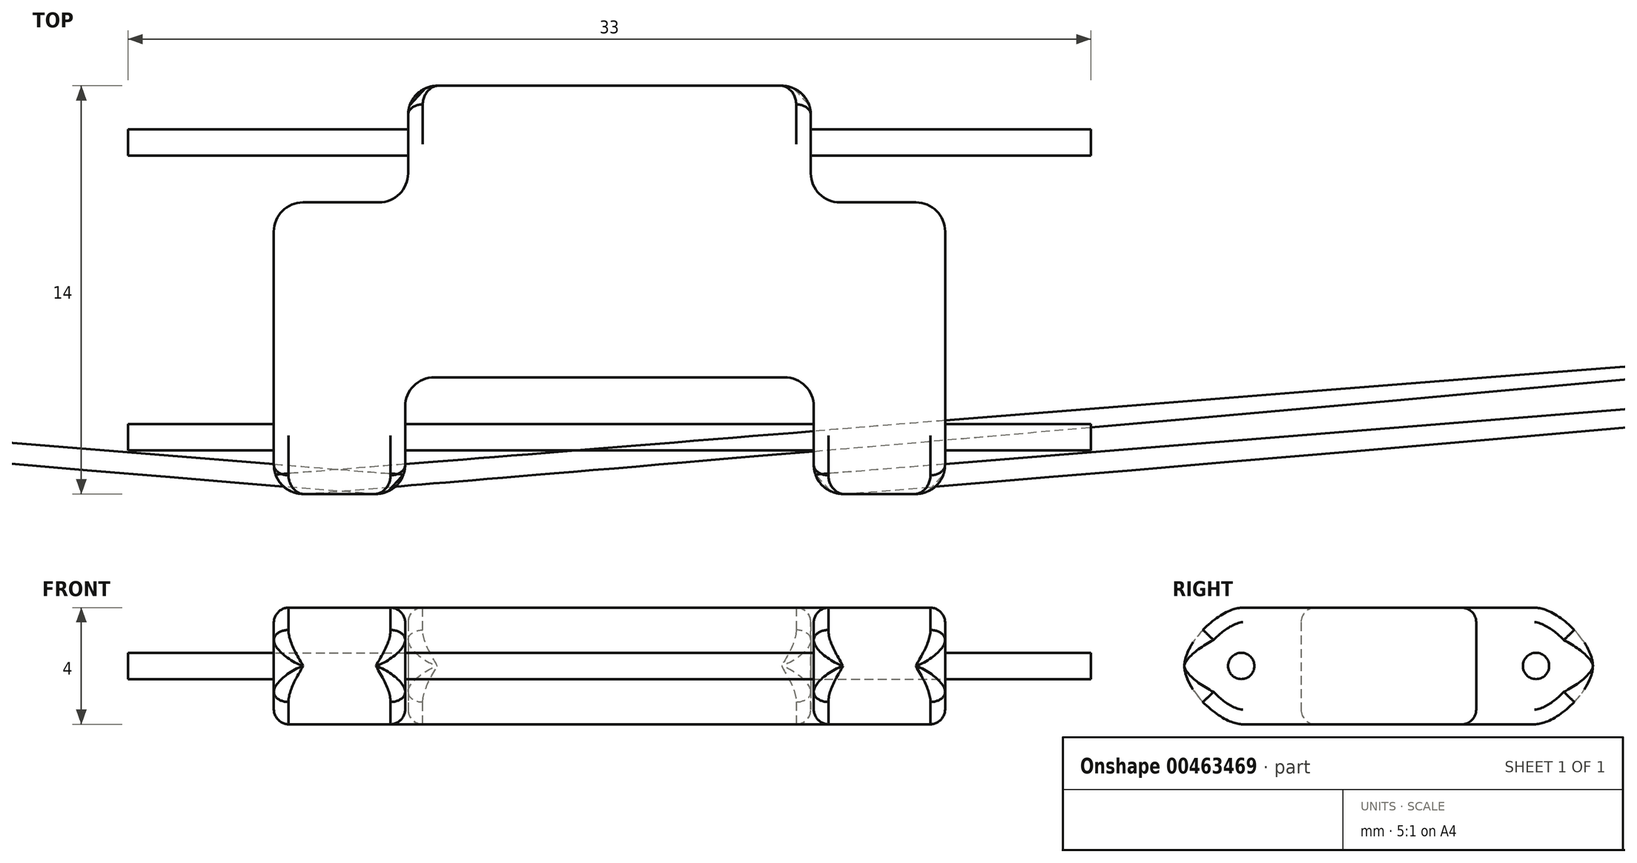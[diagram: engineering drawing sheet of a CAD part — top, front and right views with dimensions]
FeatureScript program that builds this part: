
annotation { "Feature Type Name" : "Feature", "Feature Type Description" : "" }
export const myFeature = defineFeature(function(context is Context, id is Id, definition is map)
    precondition{}
    {
        {
            var Q0;
            Q0=qCreatedBy(makeId("Top.planeOp"),FACE);
            var sketch = newSketch(context, id + "F0", { "sketchPlane" : qUnion([Q0])});
            skLineSegment(sketch, "E0", {"start": v(-1, -14) * mm, "end": v(-1, -10) * mm});
            skLineSegment(sketch, "E1", {"start": v(-1, -10) * mm, "end": v(-15, -10) * mm});
            skLineSegment(sketch, "E2", {"start": v(-15, -10) * mm, "end": v(-15, -14) * mm});
            skLineSegment(sketch, "E3", {"start": v(-15, -14) * mm, "end": v(-19.5, -14) * mm});
            skLineSegment(sketch, "E4", {"start": v(-1, -14) * mm, "end": v(3.5, -14) * mm});
            skLineSegment(sketch, "E5", {"start": v(-19.5, -14) * mm, "end": v(-19.5, -4) * mm});
            skLineSegment(sketch, "E6", {"start": v(-19.5, -4) * mm, "end": v(-14.9, -4) * mm});
            skLineSegment(sketch, "E7", {"start": v(-14.9, -4) * mm, "end": v(-14.9, 0) * mm});
            skLineSegment(sketch, "E8", {"start": v(-14.9, 0) * mm, "end": v(-1.1, 0) * mm});
            skLineSegment(sketch, "E9", {"start": v(-1.1, 0) * mm, "end": v(-1.1, -4) * mm});
            skLineSegment(sketch, "E10", {"start": v(-1.1, -4) * mm, "end": v(3.5, -4) * mm});
            skLineSegment(sketch, "E11", {"start": v(3.5, -4) * mm, "end": v(3.5, -14) * mm});
            skSolve(sketch);
        }
        {
            var Q0;
            Q0=makeQuery(id+"F0.imprint","IMPRINT",FACE,{"disambiguationData":[TD([[makeQuery(id+"F0.imprint","IMPRINT",EDGE,{"derivedFrom":sQuery(id+"F0.wireOp",EDGE,"E0")}),-1.0]])]});
            extrude(context, id + "F1", {"entities" : qUnion([Q0]), "depth" : 4 * mm, "offsetDistance" : 25 * mm});
        }
        {
            var Q0;
            Q0=makeQuery(id+"F1.opExtrude","SWEPT_EDGE",EDGE,{"disambiguationData":[OSD([sQuery(id+"F0.wireOp",EDGE,"JVpa2NSN-jCbz-SYZh-2br0-VPJ9OqO5sEDm"),sQuery(id+"F0.wireOp",EDGE,"TmuEh8Bb-qYGH-lmF9-es9h-PXmLGTj7apYS")])]});
            var Q1;
            Q1=makeQuery(id+"F1.opExtrude","SWEPT_EDGE",EDGE,{"disambiguationData":[OSD([sQuery(id+"F0.wireOp",EDGE,"Ta08JTOG-JjW1-DyQu-Rjfl-olB2hLuTZKrI"),sQuery(id+"F0.wireOp",EDGE,"5RLxsvr7-zWRq-nJ0O-23qe-XEgADmnkmLba")])]});
            var Q2;
            Q2=makeQuery(id+"F1.opExtrude","SWEPT_EDGE",EDGE,{"disambiguationData":[OSD([sQuery(id+"F0.wireOp",EDGE,"JVpa2NSN-jCbz-SYZh-2br0-VPJ9OqO5sEDm"),sQuery(id+"F0.wireOp",EDGE,"iIMMWLLX-5pRk-kAWc-YyXh-X3XYjQtiHgF8")])]});
            var Q3;
            Q3=makeQuery(id+"F1.opExtrude","SWEPT_EDGE",EDGE,{"disambiguationData":[OSD([sQuery(id+"F0.wireOp",EDGE,"Bp2VUUx9-f2Nf-Cqm2-FavC-f2X54JljXIIN"),sQuery(id+"F0.wireOp",EDGE,"TmuEh8Bb-qYGH-lmF9-es9h-PXmLGTj7apYS")])]});
            var Q4;
            Q4=makeQuery(id+"F1.opExtrude","SWEPT_EDGE",EDGE,{"disambiguationData":[OSD([sQuery(id+"F0.wireOp",EDGE,"aM0JYdi9-BpOH-c1Sx-eQZ7-4LdQcpM627Qa"),sQuery(id+"F0.wireOp",EDGE,"Ta08JTOG-JjW1-DyQu-Rjfl-olB2hLuTZKrI")])]});
            var Q5;
            Q5=makeQuery(id+"F1.opExtrude","SWEPT_EDGE",EDGE,{"disambiguationData":[OSD([sQuery(id+"F0.wireOp",EDGE,"5RLxsvr7-zWRq-nJ0O-23qe-XEgADmnkmLba"),sQuery(id+"F0.wireOp",EDGE,"Bp2VUUx9-f2Nf-Cqm2-FavC-f2X54JljXIIN")])]});
            var Q6;
            Q6=makeQuery(id+"F1.opExtrude","SWEPT_EDGE",EDGE,{"disambiguationData":[OSD([sQuery(id+"F0.wireOp",EDGE,"yeDMJLls-6pq1-5wso-vwFU-Q73Pk40JU32b"),sQuery(id+"F0.wireOp",EDGE,"aM0JYdi9-BpOH-c1Sx-eQZ7-4LdQcpM627Qa")])]});
            var Q7;
            Q7=makeQuery(id+"F1.opExtrude","SWEPT_EDGE",EDGE,{"disambiguationData":[OSD([sQuery(id+"F0.wireOp",EDGE,"yeDMJLls-6pq1-5wso-vwFU-Q73Pk40JU32b"),sQuery(id+"F0.wireOp",EDGE,"oADVPvip-QRiO-k2je-1GcM-0gCGYZzCVpqe")])]});
            var Q8;
            Q8=makeQuery(id+"F1.opExtrude","SWEPT_EDGE",EDGE,{"disambiguationData":[OSD([sQuery(id+"F0.wireOp",EDGE,"oADVPvip-QRiO-k2je-1GcM-0gCGYZzCVpqe"),sQuery(id+"F0.wireOp",EDGE,"10rlgXVg-n50c-kqx7-uExC-2RYqwfv1c7cX")])]});
            var Q9;
            Q9=makeQuery(id+"F1.opExtrude","SWEPT_EDGE",EDGE,{"disambiguationData":[OSD([sQuery(id+"F0.wireOp",EDGE,"TUznSBm0-cCe5-ovrQ-pSbA-vPagOil4q95r"),sQuery(id+"F0.wireOp",EDGE,"10rlgXVg-n50c-kqx7-uExC-2RYqwfv1c7cX")])]});
            var Q10;
            Q10=makeQuery(id+"F1.opExtrude","SWEPT_EDGE",EDGE,{"disambiguationData":[OSD([sQuery(id+"F0.wireOp",EDGE,"dIuJsfEi-w8Eu-UMFV-xWrQ-Q2fZL97E1xqK"),sQuery(id+"F0.wireOp",EDGE,"TUznSBm0-cCe5-ovrQ-pSbA-vPagOil4q95r")])]});
            var Q11;
            Q11=makeQuery(id+"F1.opExtrude","SWEPT_EDGE",EDGE,{"disambiguationData":[OSD([sQuery(id+"F0.wireOp",EDGE,"iIMMWLLX-5pRk-kAWc-YyXh-X3XYjQtiHgF8"),sQuery(id+"F0.wireOp",EDGE,"dIuJsfEi-w8Eu-UMFV-xWrQ-Q2fZL97E1xqK")])]});
            var Q12;
            Q12=makeQuery(id+"F1.opExtrude","SWEPT_EDGE",EDGE,{"disambiguationData":[OSD([sQuery(id+"F0.wireOp",EDGE,"yLF3BCVI-Jb2U-5dZP-aiB0-7200LCA53yiJ"),sQuery(id+"F0.wireOp",EDGE,"E3")])]});
            var Q13;
            Q13=makeQuery(id+"F1.opExtrude","SWEPT_EDGE",EDGE,{"disambiguationData":[OSD([sQuery(id+"F0.wireOp",EDGE,"E2"),sQuery(id+"F0.wireOp",EDGE,"E3")])]});
            var Q14;
            Q14=makeQuery(id+"F1.opExtrude","SWEPT_EDGE",EDGE,{"disambiguationData":[OSD([sQuery(id+"F0.wireOp",EDGE,"E1"),sQuery(id+"F0.wireOp",EDGE,"E2")])]});
            var Q15;
            Q15=makeQuery(id+"F1.opExtrude","SWEPT_EDGE",EDGE,{"disambiguationData":[OSD([sQuery(id+"F0.wireOp",EDGE,"E0"),sQuery(id+"F0.wireOp",EDGE,"E1")])]});
            var Q16;
            Q16=makeQuery(id+"F1.opExtrude","SWEPT_EDGE",EDGE,{"disambiguationData":[OSD([sQuery(id+"F0.wireOp",EDGE,"E0"),sQuery(id+"F0.wireOp",EDGE,"E4")])]});
            var Q17;
            Q17=makeQuery(id+"F1.opExtrude","SWEPT_EDGE",EDGE,{"disambiguationData":[OSD([sQuery(id+"F0.wireOp",EDGE,"W0sLsfjq-YAJu-qSV0-cM3q-n6XLMPe2tytr"),sQuery(id+"F0.wireOp",EDGE,"E4")])]});
            var Q18;
            Q18=makeQuery(id+"F1.opExtrude","SWEPT_EDGE",EDGE,{"disambiguationData":[OSD([sQuery(id+"F0.wireOp",EDGE,"E5"),sQuery(id+"F0.wireOp",EDGE,"E6")])]});
            var Q19;
            Q19=makeQuery(id+"F1.opExtrude","SWEPT_EDGE",EDGE,{"disambiguationData":[OSD([sQuery(id+"F0.wireOp",EDGE,"E6"),sQuery(id+"F0.wireOp",EDGE,"E7")])]});
            var Q20;
            Q20=makeQuery(id+"F1.opExtrude","SWEPT_EDGE",EDGE,{"disambiguationData":[OSD([sQuery(id+"F0.wireOp",EDGE,"E7"),sQuery(id+"F0.wireOp",EDGE,"E8")])]});
            var Q21;
            Q21=makeQuery(id+"F1.opExtrude","SWEPT_EDGE",EDGE,{"disambiguationData":[OSD([sQuery(id+"F0.wireOp",EDGE,"E8"),sQuery(id+"F0.wireOp",EDGE,"E9")])]});
            var Q22;
            Q22=makeQuery(id+"F1.opExtrude","SWEPT_EDGE",EDGE,{"disambiguationData":[OSD([sQuery(id+"F0.wireOp",EDGE,"E9"),sQuery(id+"F0.wireOp",EDGE,"E10")])]});
            var Q23;
            Q23=makeQuery(id+"F1.opExtrude","SWEPT_EDGE",EDGE,{"disambiguationData":[OSD([sQuery(id+"F0.wireOp",EDGE,"E10"),sQuery(id+"F0.wireOp",EDGE,"E11")])]});
            fillet(context, id + "F2", {"entities" : qUnion([Q0, Q1, Q2, Q3, Q4, Q5, Q6, Q7, Q8, Q9, Q10, Q11, Q12, Q13, Q14, Q15, Q16, Q17, Q18, Q19, Q20, Q21, Q22, Q23]), "radius" : 1 * mm, "tangentPropagation" : true, "allowEdgeOverflow" : false});
        }
        {
            var Q0;
            Q0=makeQuery(id+"F1.opExtrude","CAP_EDGE",EDGE,{"disambiguationData":[OSD([sQuery(id+"F0.wireOp",EDGE,"E8")])],"isStart":true});
            var Q1;
            Q1=makeQuery(id+"F1.opExtrude","CAP_EDGE",EDGE,{"disambiguationData":[OSD([sQuery(id+"F0.wireOp",EDGE,"E8")])],"isStart":false});
            var Q2;
            Q2=makeQuery(id+"F1.opExtrude","CAP_EDGE",EDGE,{"disambiguationData":[OSD([sQuery(id+"F0.wireOp",EDGE,"E3")])],"isStart":true});
            var Q3;
            Q3=makeQuery(id+"F1.opExtrude","CAP_EDGE",EDGE,{"disambiguationData":[OSD([sQuery(id+"F0.wireOp",EDGE,"E3")])],"isStart":false});
            var Q4;
            Q4=makeQuery(id+"F1.opExtrude","CAP_EDGE",EDGE,{"disambiguationData":[OSD([sQuery(id+"F0.wireOp",EDGE,"E4")])],"isStart":false});
            var Q5;
            Q5=makeQuery(id+"F1.opExtrude","CAP_EDGE",EDGE,{"disambiguationData":[OSD([sQuery(id+"F0.wireOp",EDGE,"E4")])],"isStart":true});
            fillet(context, id + "F3", {"entities" : qUnion([Q0, Q1, Q2, Q3, Q4, Q5]), "radius" : 2 * mm, "rho" : 0.3, "crossSection" : FilletCrossSection.CONIC, "allowEdgeOverflow" : false});
        }
        {
            var Q0;
            Q0=makeQuery(id+"F1.opExtrude","CAP_EDGE",EDGE,{"disambiguationData":[OSD([sQuery(id+"F0.wireOp",EDGE,"E1")])],"isStart":true});
            var Q1;
            {var subQ0=sQuery(id+"F0.wireOp",EDGE,"E2");var subQ1=sQuery(id+"F0.wireOp",EDGE,"E1");Q1=makeQuery(id+"F2.opFillet","BLEND_EDGE",EDGE,{"blendedFrom":[makeQuery(id+"F1.opExtrude","SWEPT_EDGE",EDGE,{"disambiguationData":[OSD([subQ1,subQ0])]}),makeQuery(id+"F1.opExtrude","CAP_FACE",FACE,{"disambiguationData":[OSD([sQuery(id+"F0.wireOp",EDGE,"E0"),subQ1,subQ0,sQuery(id+"F0.wireOp",EDGE,"E3"),sQuery(id+"F0.wireOp",EDGE,"E4"),sQuery(id+"F0.wireOp",EDGE,"E5"),sQuery(id+"F0.wireOp",EDGE,"E6"),sQuery(id+"F0.wireOp",EDGE,"E7"),sQuery(id+"F0.wireOp",EDGE,"E8"),sQuery(id+"F0.wireOp",EDGE,"E9"),sQuery(id+"F0.wireOp",EDGE,"E10"),sQuery(id+"F0.wireOp",EDGE,"E11")])],"isStart":true})],"blendedInto":[makeQuery(id+"F1.opExtrude","CAP_FACE",FACE,{"disambiguationData":[OSD([sQuery(id+"F0.wireOp",EDGE,"E0"),subQ1,subQ0,sQuery(id+"F0.wireOp",EDGE,"E3"),sQuery(id+"F0.wireOp",EDGE,"E4"),sQuery(id+"F0.wireOp",EDGE,"E5"),sQuery(id+"F0.wireOp",EDGE,"E6"),sQuery(id+"F0.wireOp",EDGE,"E7"),sQuery(id+"F0.wireOp",EDGE,"E8"),sQuery(id+"F0.wireOp",EDGE,"E9"),sQuery(id+"F0.wireOp",EDGE,"E10"),sQuery(id+"F0.wireOp",EDGE,"E11")])],"isStart":true})]});}
            var Q2;
            Q2=makeQuery(id+"F1.opExtrude","CAP_EDGE",EDGE,{"disambiguationData":[OSD([sQuery(id+"F0.wireOp",EDGE,"E2")])],"isStart":true});
            var Q3;
            Q3=makeQuery(id+"F3.opFillet","BLEND_EDGE",EDGE,{"blendedFrom":[makeQuery(id+"F1.opExtrude","CAP_EDGE",EDGE,{"disambiguationData":[OSD([sQuery(id+"F0.wireOp",EDGE,"E3")])],"isStart":true}),makeQuery(id+"F1.opExtrude","SWEPT_FACE",FACE,{"disambiguationData":[OSD([sQuery(id+"F0.wireOp",EDGE,"E2")])]})],"blendedInto":[makeQuery(id+"F1.opExtrude","SWEPT_FACE",FACE,{"disambiguationData":[OSD([sQuery(id+"F0.wireOp",EDGE,"E2")])]})]});
            var Q4;
            {var subQ0=sQuery(id+"F0.wireOp",EDGE,"E3");Q4=makeQuery(id+"F3.opFillet","BLEND_EDGE",EDGE,{"blendedFrom":[makeQuery(id+"F1.opExtrude","CAP_EDGE",EDGE,{"disambiguationData":[OSD([subQ0])],"isStart":true}),makeQuery(id+"F2.opFillet","BLEND_FACE",FACE,{"disambiguationData":[OSD([sQuery(id+"F0.wireOp",EDGE,"E2"),subQ0])]})],"blendedInto":[makeQuery(id+"F2.opFillet","BLEND_FACE",FACE,{"disambiguationData":[OSD([sQuery(id+"F0.wireOp",EDGE,"E2"),subQ0])]})]});}
            var Q5;
            {var subQ0=sQuery(id+"F0.wireOp",EDGE,"E1");var subQ1=sQuery(id+"F0.wireOp",EDGE,"E0");Q5=makeQuery(id+"F2.opFillet","BLEND_EDGE",EDGE,{"blendedFrom":[makeQuery(id+"F1.opExtrude","SWEPT_EDGE",EDGE,{"disambiguationData":[OSD([subQ1,subQ0])]}),makeQuery(id+"F1.opExtrude","CAP_FACE",FACE,{"disambiguationData":[OSD([subQ1,subQ0,sQuery(id+"F0.wireOp",EDGE,"E2"),sQuery(id+"F0.wireOp",EDGE,"E3"),sQuery(id+"F0.wireOp",EDGE,"E4"),sQuery(id+"F0.wireOp",EDGE,"E5"),sQuery(id+"F0.wireOp",EDGE,"E6"),sQuery(id+"F0.wireOp",EDGE,"E7"),sQuery(id+"F0.wireOp",EDGE,"E8"),sQuery(id+"F0.wireOp",EDGE,"E9"),sQuery(id+"F0.wireOp",EDGE,"E10"),sQuery(id+"F0.wireOp",EDGE,"E11")])],"isStart":true})],"blendedInto":[makeQuery(id+"F1.opExtrude","CAP_FACE",FACE,{"disambiguationData":[OSD([subQ1,subQ0,sQuery(id+"F0.wireOp",EDGE,"E2"),sQuery(id+"F0.wireOp",EDGE,"E3"),sQuery(id+"F0.wireOp",EDGE,"E4"),sQuery(id+"F0.wireOp",EDGE,"E5"),sQuery(id+"F0.wireOp",EDGE,"E6"),sQuery(id+"F0.wireOp",EDGE,"E7"),sQuery(id+"F0.wireOp",EDGE,"E8"),sQuery(id+"F0.wireOp",EDGE,"E9"),sQuery(id+"F0.wireOp",EDGE,"E10"),sQuery(id+"F0.wireOp",EDGE,"E11")])],"isStart":true})]});}
            var Q6;
            Q6=makeQuery(id+"F1.opExtrude","CAP_EDGE",EDGE,{"disambiguationData":[OSD([sQuery(id+"F0.wireOp",EDGE,"E0")])],"isStart":true});
            var Q7;
            {var subQ0=sQuery(id+"F0.wireOp",EDGE,"E4");Q7=makeQuery(id+"F3.opFillet","BLEND_EDGE",EDGE,{"blendedFrom":[makeQuery(id+"F1.opExtrude","CAP_EDGE",EDGE,{"disambiguationData":[OSD([subQ0])],"isStart":true}),makeQuery(id+"F2.opFillet","BLEND_FACE",FACE,{"disambiguationData":[OSD([sQuery(id+"F0.wireOp",EDGE,"E0"),subQ0])]})],"blendedInto":[makeQuery(id+"F2.opFillet","BLEND_FACE",FACE,{"disambiguationData":[OSD([sQuery(id+"F0.wireOp",EDGE,"E0"),subQ0])]})]});}
            var Q8;
            {var subQ0=sQuery(id+"F0.wireOp",EDGE,"E4");Q8=makeQuery(id+"F3.opFillet","BLEND_EDGE",EDGE,{"blendedFrom":[makeQuery(id+"F1.opExtrude","CAP_EDGE",EDGE,{"disambiguationData":[OSD([subQ0])],"isStart":false}),makeQuery(id+"F2.opFillet","BLEND_FACE",FACE,{"disambiguationData":[OSD([sQuery(id+"F0.wireOp",EDGE,"E0"),subQ0])]})],"blendedInto":[makeQuery(id+"F2.opFillet","BLEND_FACE",FACE,{"disambiguationData":[OSD([sQuery(id+"F0.wireOp",EDGE,"E0"),subQ0])]})]});}
            var Q9;
            {var subQ0=sQuery(id+"F0.wireOp",EDGE,"E3");Q9=makeQuery(id+"F3.opFillet","BLEND_EDGE",EDGE,{"blendedFrom":[makeQuery(id+"F1.opExtrude","CAP_EDGE",EDGE,{"disambiguationData":[OSD([subQ0])],"isStart":false}),makeQuery(id+"F2.opFillet","BLEND_FACE",FACE,{"disambiguationData":[OSD([sQuery(id+"F0.wireOp",EDGE,"E2"),subQ0])]})],"blendedInto":[makeQuery(id+"F2.opFillet","BLEND_FACE",FACE,{"disambiguationData":[OSD([sQuery(id+"F0.wireOp",EDGE,"E2"),subQ0])]})]});}
            var Q10;
            Q10=makeQuery(id+"F3.opFillet","BLEND_EDGE",EDGE,{"blendedFrom":[makeQuery(id+"F1.opExtrude","CAP_EDGE",EDGE,{"disambiguationData":[OSD([sQuery(id+"F0.wireOp",EDGE,"E3")])],"isStart":false}),makeQuery(id+"F1.opExtrude","SWEPT_FACE",FACE,{"disambiguationData":[OSD([sQuery(id+"F0.wireOp",EDGE,"E2")])]})],"blendedInto":[makeQuery(id+"F1.opExtrude","SWEPT_FACE",FACE,{"disambiguationData":[OSD([sQuery(id+"F0.wireOp",EDGE,"E2")])]})]});
            var Q11;
            Q11=makeQuery(id+"F1.opExtrude","CAP_EDGE",EDGE,{"disambiguationData":[OSD([sQuery(id+"F0.wireOp",EDGE,"E2")])],"isStart":false});
            var Q12;
            {var subQ0=sQuery(id+"F0.wireOp",EDGE,"E2");var subQ1=sQuery(id+"F0.wireOp",EDGE,"E1");Q12=makeQuery(id+"F2.opFillet","BLEND_EDGE",EDGE,{"blendedFrom":[makeQuery(id+"F1.opExtrude","SWEPT_EDGE",EDGE,{"disambiguationData":[OSD([subQ1,subQ0])]}),makeQuery(id+"F1.opExtrude","CAP_FACE",FACE,{"disambiguationData":[OSD([sQuery(id+"F0.wireOp",EDGE,"E0"),subQ1,subQ0,sQuery(id+"F0.wireOp",EDGE,"E3"),sQuery(id+"F0.wireOp",EDGE,"E4"),sQuery(id+"F0.wireOp",EDGE,"E5"),sQuery(id+"F0.wireOp",EDGE,"E6"),sQuery(id+"F0.wireOp",EDGE,"E7"),sQuery(id+"F0.wireOp",EDGE,"E8"),sQuery(id+"F0.wireOp",EDGE,"E9"),sQuery(id+"F0.wireOp",EDGE,"E10"),sQuery(id+"F0.wireOp",EDGE,"E11")])],"isStart":false})],"blendedInto":[makeQuery(id+"F1.opExtrude","CAP_FACE",FACE,{"disambiguationData":[OSD([sQuery(id+"F0.wireOp",EDGE,"E0"),subQ1,subQ0,sQuery(id+"F0.wireOp",EDGE,"E3"),sQuery(id+"F0.wireOp",EDGE,"E4"),sQuery(id+"F0.wireOp",EDGE,"E5"),sQuery(id+"F0.wireOp",EDGE,"E6"),sQuery(id+"F0.wireOp",EDGE,"E7"),sQuery(id+"F0.wireOp",EDGE,"E8"),sQuery(id+"F0.wireOp",EDGE,"E9"),sQuery(id+"F0.wireOp",EDGE,"E10"),sQuery(id+"F0.wireOp",EDGE,"E11")])],"isStart":false})]});}
            var Q13;
            Q13=makeQuery(id+"F1.opExtrude","CAP_EDGE",EDGE,{"disambiguationData":[OSD([sQuery(id+"F0.wireOp",EDGE,"E1")])],"isStart":false});
            var Q14;
            {var subQ0=sQuery(id+"F0.wireOp",EDGE,"E1");var subQ1=sQuery(id+"F0.wireOp",EDGE,"E0");Q14=makeQuery(id+"F2.opFillet","BLEND_EDGE",EDGE,{"blendedFrom":[makeQuery(id+"F1.opExtrude","SWEPT_EDGE",EDGE,{"disambiguationData":[OSD([subQ1,subQ0])]}),makeQuery(id+"F1.opExtrude","CAP_FACE",FACE,{"disambiguationData":[OSD([subQ1,subQ0,sQuery(id+"F0.wireOp",EDGE,"E2"),sQuery(id+"F0.wireOp",EDGE,"E3"),sQuery(id+"F0.wireOp",EDGE,"E4"),sQuery(id+"F0.wireOp",EDGE,"E5"),sQuery(id+"F0.wireOp",EDGE,"E6"),sQuery(id+"F0.wireOp",EDGE,"E7"),sQuery(id+"F0.wireOp",EDGE,"E8"),sQuery(id+"F0.wireOp",EDGE,"E9"),sQuery(id+"F0.wireOp",EDGE,"E10"),sQuery(id+"F0.wireOp",EDGE,"E11")])],"isStart":false})],"blendedInto":[makeQuery(id+"F1.opExtrude","CAP_FACE",FACE,{"disambiguationData":[OSD([subQ1,subQ0,sQuery(id+"F0.wireOp",EDGE,"E2"),sQuery(id+"F0.wireOp",EDGE,"E3"),sQuery(id+"F0.wireOp",EDGE,"E4"),sQuery(id+"F0.wireOp",EDGE,"E5"),sQuery(id+"F0.wireOp",EDGE,"E6"),sQuery(id+"F0.wireOp",EDGE,"E7"),sQuery(id+"F0.wireOp",EDGE,"E8"),sQuery(id+"F0.wireOp",EDGE,"E9"),sQuery(id+"F0.wireOp",EDGE,"E10"),sQuery(id+"F0.wireOp",EDGE,"E11")])],"isStart":false})]});}
            var Q15;
            Q15=makeQuery(id+"F1.opExtrude","CAP_EDGE",EDGE,{"disambiguationData":[OSD([sQuery(id+"F0.wireOp",EDGE,"E0")])],"isStart":false});
            var Q16;
            Q16=makeQuery(id+"F3.opFillet","BLEND_EDGE",EDGE,{"blendedFrom":[makeQuery(id+"F1.opExtrude","CAP_EDGE",EDGE,{"disambiguationData":[OSD([sQuery(id+"F0.wireOp",EDGE,"E4")])],"isStart":false}),makeQuery(id+"F1.opExtrude","SWEPT_FACE",FACE,{"disambiguationData":[OSD([sQuery(id+"F0.wireOp",EDGE,"E0")])]})],"blendedInto":[makeQuery(id+"F1.opExtrude","SWEPT_FACE",FACE,{"disambiguationData":[OSD([sQuery(id+"F0.wireOp",EDGE,"E0")])]})]});
            var Q17;
            Q17=makeQuery(id+"F3.opFillet","BLEND_EDGE",EDGE,{"blendedFrom":[makeQuery(id+"F1.opExtrude","CAP_EDGE",EDGE,{"disambiguationData":[OSD([sQuery(id+"F0.wireOp",EDGE,"E4")])],"isStart":true}),makeQuery(id+"F1.opExtrude","SWEPT_FACE",FACE,{"disambiguationData":[OSD([sQuery(id+"F0.wireOp",EDGE,"E0")])]})],"blendedInto":[makeQuery(id+"F1.opExtrude","SWEPT_FACE",FACE,{"disambiguationData":[OSD([sQuery(id+"F0.wireOp",EDGE,"E0")])]})]});
            var Q18;
            {var subQ0=sQuery(id+"F0.wireOp",EDGE,"E3");Q18=makeQuery(id+"F3.opFillet","BLEND_EDGE",EDGE,{"blendedFrom":[makeQuery(id+"F1.opExtrude","CAP_EDGE",EDGE,{"disambiguationData":[OSD([subQ0])],"isStart":false}),makeQuery(id+"F2.opFillet","BLEND_FACE",FACE,{"disambiguationData":[OSD([subQ0,sQuery(id+"F0.wireOp",EDGE,"E5")])]})],"blendedInto":[makeQuery(id+"F2.opFillet","BLEND_FACE",FACE,{"disambiguationData":[OSD([subQ0,sQuery(id+"F0.wireOp",EDGE,"E5")])]})]});}
            var Q19;
            {var subQ0=sQuery(id+"F0.wireOp",EDGE,"E3");Q19=makeQuery(id+"F3.opFillet","BLEND_EDGE",EDGE,{"blendedFrom":[makeQuery(id+"F1.opExtrude","CAP_EDGE",EDGE,{"disambiguationData":[OSD([subQ0])],"isStart":true}),makeQuery(id+"F2.opFillet","BLEND_FACE",FACE,{"disambiguationData":[OSD([subQ0,sQuery(id+"F0.wireOp",EDGE,"E5")])]})],"blendedInto":[makeQuery(id+"F2.opFillet","BLEND_FACE",FACE,{"disambiguationData":[OSD([subQ0,sQuery(id+"F0.wireOp",EDGE,"E5")])]})]});}
            var Q20;
            Q20=makeQuery(id+"F1.opExtrude","CAP_EDGE",EDGE,{"disambiguationData":[OSD([sQuery(id+"F0.wireOp",EDGE,"E5")])],"isStart":true});
            var Q21;
            Q21=makeQuery(id+"F3.opFillet","BLEND_EDGE",EDGE,{"blendedFrom":[makeQuery(id+"F1.opExtrude","CAP_EDGE",EDGE,{"disambiguationData":[OSD([sQuery(id+"F0.wireOp",EDGE,"E3")])],"isStart":true}),makeQuery(id+"F1.opExtrude","SWEPT_FACE",FACE,{"disambiguationData":[OSD([sQuery(id+"F0.wireOp",EDGE,"E5")])]})],"blendedInto":[makeQuery(id+"F1.opExtrude","SWEPT_FACE",FACE,{"disambiguationData":[OSD([sQuery(id+"F0.wireOp",EDGE,"E5")])]})]});
            var Q22;
            Q22=makeQuery(id+"F3.opFillet","BLEND_EDGE",EDGE,{"blendedFrom":[makeQuery(id+"F1.opExtrude","CAP_EDGE",EDGE,{"disambiguationData":[OSD([sQuery(id+"F0.wireOp",EDGE,"E3")])],"isStart":false}),makeQuery(id+"F1.opExtrude","SWEPT_FACE",FACE,{"disambiguationData":[OSD([sQuery(id+"F0.wireOp",EDGE,"E5")])]})],"blendedInto":[makeQuery(id+"F1.opExtrude","SWEPT_FACE",FACE,{"disambiguationData":[OSD([sQuery(id+"F0.wireOp",EDGE,"E5")])]})]});
            var Q23;
            Q23=makeQuery(id+"F1.opExtrude","CAP_EDGE",EDGE,{"disambiguationData":[OSD([sQuery(id+"F0.wireOp",EDGE,"E5")])],"isStart":false});
            var Q24;
            {var subQ0=sQuery(id+"F0.wireOp",EDGE,"E6");var subQ1=sQuery(id+"F0.wireOp",EDGE,"E5");Q24=makeQuery(id+"F2.opFillet","BLEND_EDGE",EDGE,{"blendedFrom":[makeQuery(id+"F1.opExtrude","SWEPT_EDGE",EDGE,{"disambiguationData":[OSD([subQ1,subQ0])]}),makeQuery(id+"F1.opExtrude","CAP_FACE",FACE,{"disambiguationData":[OSD([sQuery(id+"F0.wireOp",EDGE,"E0"),sQuery(id+"F0.wireOp",EDGE,"E1"),sQuery(id+"F0.wireOp",EDGE,"E2"),sQuery(id+"F0.wireOp",EDGE,"E3"),sQuery(id+"F0.wireOp",EDGE,"E4"),subQ1,subQ0,sQuery(id+"F0.wireOp",EDGE,"E7"),sQuery(id+"F0.wireOp",EDGE,"E8"),sQuery(id+"F0.wireOp",EDGE,"E9"),sQuery(id+"F0.wireOp",EDGE,"E10"),sQuery(id+"F0.wireOp",EDGE,"E11")])],"isStart":false})],"blendedInto":[makeQuery(id+"F1.opExtrude","CAP_FACE",FACE,{"disambiguationData":[OSD([sQuery(id+"F0.wireOp",EDGE,"E0"),sQuery(id+"F0.wireOp",EDGE,"E1"),sQuery(id+"F0.wireOp",EDGE,"E2"),sQuery(id+"F0.wireOp",EDGE,"E3"),sQuery(id+"F0.wireOp",EDGE,"E4"),subQ1,subQ0,sQuery(id+"F0.wireOp",EDGE,"E7"),sQuery(id+"F0.wireOp",EDGE,"E8"),sQuery(id+"F0.wireOp",EDGE,"E9"),sQuery(id+"F0.wireOp",EDGE,"E10"),sQuery(id+"F0.wireOp",EDGE,"E11")])],"isStart":false})]});}
            var Q25;
            {var subQ0=sQuery(id+"F0.wireOp",EDGE,"E6");var subQ1=sQuery(id+"F0.wireOp",EDGE,"E5");Q25=makeQuery(id+"F2.opFillet","BLEND_EDGE",EDGE,{"blendedFrom":[makeQuery(id+"F1.opExtrude","SWEPT_EDGE",EDGE,{"disambiguationData":[OSD([subQ1,subQ0])]}),makeQuery(id+"F1.opExtrude","CAP_FACE",FACE,{"disambiguationData":[OSD([sQuery(id+"F0.wireOp",EDGE,"E0"),sQuery(id+"F0.wireOp",EDGE,"E1"),sQuery(id+"F0.wireOp",EDGE,"E2"),sQuery(id+"F0.wireOp",EDGE,"E3"),sQuery(id+"F0.wireOp",EDGE,"E4"),subQ1,subQ0,sQuery(id+"F0.wireOp",EDGE,"E7"),sQuery(id+"F0.wireOp",EDGE,"E8"),sQuery(id+"F0.wireOp",EDGE,"E9"),sQuery(id+"F0.wireOp",EDGE,"E10"),sQuery(id+"F0.wireOp",EDGE,"E11")])],"isStart":true})],"blendedInto":[makeQuery(id+"F1.opExtrude","CAP_FACE",FACE,{"disambiguationData":[OSD([sQuery(id+"F0.wireOp",EDGE,"E0"),sQuery(id+"F0.wireOp",EDGE,"E1"),sQuery(id+"F0.wireOp",EDGE,"E2"),sQuery(id+"F0.wireOp",EDGE,"E3"),sQuery(id+"F0.wireOp",EDGE,"E4"),subQ1,subQ0,sQuery(id+"F0.wireOp",EDGE,"E7"),sQuery(id+"F0.wireOp",EDGE,"E8"),sQuery(id+"F0.wireOp",EDGE,"E9"),sQuery(id+"F0.wireOp",EDGE,"E10"),sQuery(id+"F0.wireOp",EDGE,"E11")])],"isStart":true})]});}
            var Q26;
            Q26=makeQuery(id+"F1.opExtrude","CAP_EDGE",EDGE,{"disambiguationData":[OSD([sQuery(id+"F0.wireOp",EDGE,"E6")])],"isStart":true});
            var Q27;
            Q27=makeQuery(id+"F1.opExtrude","CAP_EDGE",EDGE,{"disambiguationData":[OSD([sQuery(id+"F0.wireOp",EDGE,"E6")])],"isStart":false});
            var Q28;
            {var subQ0=sQuery(id+"F0.wireOp",EDGE,"E7");var subQ1=sQuery(id+"F0.wireOp",EDGE,"E6");Q28=makeQuery(id+"F2.opFillet","BLEND_EDGE",EDGE,{"blendedFrom":[makeQuery(id+"F1.opExtrude","SWEPT_EDGE",EDGE,{"disambiguationData":[OSD([subQ1,subQ0])]}),makeQuery(id+"F1.opExtrude","CAP_FACE",FACE,{"disambiguationData":[OSD([sQuery(id+"F0.wireOp",EDGE,"E0"),sQuery(id+"F0.wireOp",EDGE,"E1"),sQuery(id+"F0.wireOp",EDGE,"E2"),sQuery(id+"F0.wireOp",EDGE,"E3"),sQuery(id+"F0.wireOp",EDGE,"E4"),sQuery(id+"F0.wireOp",EDGE,"E5"),subQ1,subQ0,sQuery(id+"F0.wireOp",EDGE,"E8"),sQuery(id+"F0.wireOp",EDGE,"E9"),sQuery(id+"F0.wireOp",EDGE,"E10"),sQuery(id+"F0.wireOp",EDGE,"E11")])],"isStart":false})],"blendedInto":[makeQuery(id+"F1.opExtrude","CAP_FACE",FACE,{"disambiguationData":[OSD([sQuery(id+"F0.wireOp",EDGE,"E0"),sQuery(id+"F0.wireOp",EDGE,"E1"),sQuery(id+"F0.wireOp",EDGE,"E2"),sQuery(id+"F0.wireOp",EDGE,"E3"),sQuery(id+"F0.wireOp",EDGE,"E4"),sQuery(id+"F0.wireOp",EDGE,"E5"),subQ1,subQ0,sQuery(id+"F0.wireOp",EDGE,"E8"),sQuery(id+"F0.wireOp",EDGE,"E9"),sQuery(id+"F0.wireOp",EDGE,"E10"),sQuery(id+"F0.wireOp",EDGE,"E11")])],"isStart":false})]});}
            var Q29;
            {var subQ0=sQuery(id+"F0.wireOp",EDGE,"E7");var subQ1=sQuery(id+"F0.wireOp",EDGE,"E6");Q29=makeQuery(id+"F2.opFillet","BLEND_EDGE",EDGE,{"blendedFrom":[makeQuery(id+"F1.opExtrude","SWEPT_EDGE",EDGE,{"disambiguationData":[OSD([subQ1,subQ0])]}),makeQuery(id+"F1.opExtrude","CAP_FACE",FACE,{"disambiguationData":[OSD([sQuery(id+"F0.wireOp",EDGE,"E0"),sQuery(id+"F0.wireOp",EDGE,"E1"),sQuery(id+"F0.wireOp",EDGE,"E2"),sQuery(id+"F0.wireOp",EDGE,"E3"),sQuery(id+"F0.wireOp",EDGE,"E4"),sQuery(id+"F0.wireOp",EDGE,"E5"),subQ1,subQ0,sQuery(id+"F0.wireOp",EDGE,"E8"),sQuery(id+"F0.wireOp",EDGE,"E9"),sQuery(id+"F0.wireOp",EDGE,"E10"),sQuery(id+"F0.wireOp",EDGE,"E11")])],"isStart":true})],"blendedInto":[makeQuery(id+"F1.opExtrude","CAP_FACE",FACE,{"disambiguationData":[OSD([sQuery(id+"F0.wireOp",EDGE,"E0"),sQuery(id+"F0.wireOp",EDGE,"E1"),sQuery(id+"F0.wireOp",EDGE,"E2"),sQuery(id+"F0.wireOp",EDGE,"E3"),sQuery(id+"F0.wireOp",EDGE,"E4"),sQuery(id+"F0.wireOp",EDGE,"E5"),subQ1,subQ0,sQuery(id+"F0.wireOp",EDGE,"E8"),sQuery(id+"F0.wireOp",EDGE,"E9"),sQuery(id+"F0.wireOp",EDGE,"E10"),sQuery(id+"F0.wireOp",EDGE,"E11")])],"isStart":true})]});}
            var Q30;
            Q30=makeQuery(id+"F3.opFillet","BLEND_EDGE",EDGE,{"blendedFrom":[makeQuery(id+"F1.opExtrude","CAP_EDGE",EDGE,{"disambiguationData":[OSD([sQuery(id+"F0.wireOp",EDGE,"E8")])],"isStart":false}),makeQuery(id+"F1.opExtrude","SWEPT_FACE",FACE,{"disambiguationData":[OSD([sQuery(id+"F0.wireOp",EDGE,"E7")])]})],"blendedInto":[makeQuery(id+"F1.opExtrude","SWEPT_FACE",FACE,{"disambiguationData":[OSD([sQuery(id+"F0.wireOp",EDGE,"E7")])]})]});
            var Q31;
            Q31=makeQuery(id+"F1.opExtrude","CAP_EDGE",EDGE,{"disambiguationData":[OSD([sQuery(id+"F0.wireOp",EDGE,"E7")])],"isStart":false});
            var Q32;
            {var subQ0=sQuery(id+"F0.wireOp",EDGE,"E8");Q32=makeQuery(id+"F3.opFillet","BLEND_EDGE",EDGE,{"blendedFrom":[makeQuery(id+"F1.opExtrude","CAP_EDGE",EDGE,{"disambiguationData":[OSD([subQ0])],"isStart":false}),makeQuery(id+"F2.opFillet","BLEND_FACE",FACE,{"disambiguationData":[OSD([sQuery(id+"F0.wireOp",EDGE,"E7"),subQ0])]})],"blendedInto":[makeQuery(id+"F2.opFillet","BLEND_FACE",FACE,{"disambiguationData":[OSD([sQuery(id+"F0.wireOp",EDGE,"E7"),subQ0])]})]});}
            var Q33;
            {var subQ0=sQuery(id+"F0.wireOp",EDGE,"E8");Q33=makeQuery(id+"F3.opFillet","BLEND_EDGE",EDGE,{"blendedFrom":[makeQuery(id+"F1.opExtrude","CAP_EDGE",EDGE,{"disambiguationData":[OSD([subQ0])],"isStart":true}),makeQuery(id+"F2.opFillet","BLEND_FACE",FACE,{"disambiguationData":[OSD([sQuery(id+"F0.wireOp",EDGE,"E7"),subQ0])]})],"blendedInto":[makeQuery(id+"F2.opFillet","BLEND_FACE",FACE,{"disambiguationData":[OSD([sQuery(id+"F0.wireOp",EDGE,"E7"),subQ0])]})]});}
            var Q34;
            Q34=makeQuery(id+"F3.opFillet","BLEND_EDGE",EDGE,{"blendedFrom":[makeQuery(id+"F1.opExtrude","CAP_EDGE",EDGE,{"disambiguationData":[OSD([sQuery(id+"F0.wireOp",EDGE,"E8")])],"isStart":true}),makeQuery(id+"F1.opExtrude","SWEPT_FACE",FACE,{"disambiguationData":[OSD([sQuery(id+"F0.wireOp",EDGE,"E7")])]})],"blendedInto":[makeQuery(id+"F1.opExtrude","SWEPT_FACE",FACE,{"disambiguationData":[OSD([sQuery(id+"F0.wireOp",EDGE,"E7")])]})]});
            var Q35;
            Q35=makeQuery(id+"F1.opExtrude","CAP_EDGE",EDGE,{"disambiguationData":[OSD([sQuery(id+"F0.wireOp",EDGE,"E7")])],"isStart":true});
            var Q36;
            {var subQ0=sQuery(id+"F0.wireOp",EDGE,"E8");Q36=makeQuery(id+"F3.opFillet","BLEND_EDGE",EDGE,{"blendedFrom":[makeQuery(id+"F1.opExtrude","CAP_EDGE",EDGE,{"disambiguationData":[OSD([subQ0])],"isStart":true}),makeQuery(id+"F2.opFillet","BLEND_FACE",FACE,{"disambiguationData":[OSD([subQ0,sQuery(id+"F0.wireOp",EDGE,"E9")])]})],"blendedInto":[makeQuery(id+"F2.opFillet","BLEND_FACE",FACE,{"disambiguationData":[OSD([subQ0,sQuery(id+"F0.wireOp",EDGE,"E9")])]})]});}
            var Q37;
            Q37=makeQuery(id+"F3.opFillet","BLEND_EDGE",EDGE,{"blendedFrom":[makeQuery(id+"F1.opExtrude","CAP_EDGE",EDGE,{"disambiguationData":[OSD([sQuery(id+"F0.wireOp",EDGE,"E8")])],"isStart":true}),makeQuery(id+"F1.opExtrude","SWEPT_FACE",FACE,{"disambiguationData":[OSD([sQuery(id+"F0.wireOp",EDGE,"E9")])]})],"blendedInto":[makeQuery(id+"F1.opExtrude","SWEPT_FACE",FACE,{"disambiguationData":[OSD([sQuery(id+"F0.wireOp",EDGE,"E9")])]})]});
            var Q38;
            Q38=makeQuery(id+"F1.opExtrude","CAP_EDGE",EDGE,{"disambiguationData":[OSD([sQuery(id+"F0.wireOp",EDGE,"E9")])],"isStart":true});
            var Q39;
            {var subQ0=sQuery(id+"F0.wireOp",EDGE,"E10");var subQ1=sQuery(id+"F0.wireOp",EDGE,"E9");Q39=makeQuery(id+"F2.opFillet","BLEND_EDGE",EDGE,{"blendedFrom":[makeQuery(id+"F1.opExtrude","SWEPT_EDGE",EDGE,{"disambiguationData":[OSD([subQ1,subQ0])]}),makeQuery(id+"F1.opExtrude","CAP_FACE",FACE,{"disambiguationData":[OSD([sQuery(id+"F0.wireOp",EDGE,"E0"),sQuery(id+"F0.wireOp",EDGE,"E1"),sQuery(id+"F0.wireOp",EDGE,"E2"),sQuery(id+"F0.wireOp",EDGE,"E3"),sQuery(id+"F0.wireOp",EDGE,"E4"),sQuery(id+"F0.wireOp",EDGE,"E5"),sQuery(id+"F0.wireOp",EDGE,"E6"),sQuery(id+"F0.wireOp",EDGE,"E7"),sQuery(id+"F0.wireOp",EDGE,"E8"),subQ1,subQ0,sQuery(id+"F0.wireOp",EDGE,"E11")])],"isStart":true})],"blendedInto":[makeQuery(id+"F1.opExtrude","CAP_FACE",FACE,{"disambiguationData":[OSD([sQuery(id+"F0.wireOp",EDGE,"E0"),sQuery(id+"F0.wireOp",EDGE,"E1"),sQuery(id+"F0.wireOp",EDGE,"E2"),sQuery(id+"F0.wireOp",EDGE,"E3"),sQuery(id+"F0.wireOp",EDGE,"E4"),sQuery(id+"F0.wireOp",EDGE,"E5"),sQuery(id+"F0.wireOp",EDGE,"E6"),sQuery(id+"F0.wireOp",EDGE,"E7"),sQuery(id+"F0.wireOp",EDGE,"E8"),subQ1,subQ0,sQuery(id+"F0.wireOp",EDGE,"E11")])],"isStart":true})]});}
            var Q40;
            Q40=makeQuery(id+"F1.opExtrude","CAP_EDGE",EDGE,{"disambiguationData":[OSD([sQuery(id+"F0.wireOp",EDGE,"E10")])],"isStart":true});
            var Q41;
            {var subQ0=sQuery(id+"F0.wireOp",EDGE,"E11");var subQ1=sQuery(id+"F0.wireOp",EDGE,"E10");Q41=makeQuery(id+"F2.opFillet","BLEND_EDGE",EDGE,{"blendedFrom":[makeQuery(id+"F1.opExtrude","SWEPT_EDGE",EDGE,{"disambiguationData":[OSD([subQ1,subQ0])]}),makeQuery(id+"F1.opExtrude","CAP_FACE",FACE,{"disambiguationData":[OSD([sQuery(id+"F0.wireOp",EDGE,"E0"),sQuery(id+"F0.wireOp",EDGE,"E1"),sQuery(id+"F0.wireOp",EDGE,"E2"),sQuery(id+"F0.wireOp",EDGE,"E3"),sQuery(id+"F0.wireOp",EDGE,"E4"),sQuery(id+"F0.wireOp",EDGE,"E5"),sQuery(id+"F0.wireOp",EDGE,"E6"),sQuery(id+"F0.wireOp",EDGE,"E7"),sQuery(id+"F0.wireOp",EDGE,"E8"),sQuery(id+"F0.wireOp",EDGE,"E9"),subQ1,subQ0])],"isStart":true})],"blendedInto":[makeQuery(id+"F1.opExtrude","CAP_FACE",FACE,{"disambiguationData":[OSD([sQuery(id+"F0.wireOp",EDGE,"E0"),sQuery(id+"F0.wireOp",EDGE,"E1"),sQuery(id+"F0.wireOp",EDGE,"E2"),sQuery(id+"F0.wireOp",EDGE,"E3"),sQuery(id+"F0.wireOp",EDGE,"E4"),sQuery(id+"F0.wireOp",EDGE,"E5"),sQuery(id+"F0.wireOp",EDGE,"E6"),sQuery(id+"F0.wireOp",EDGE,"E7"),sQuery(id+"F0.wireOp",EDGE,"E8"),sQuery(id+"F0.wireOp",EDGE,"E9"),subQ1,subQ0])],"isStart":true})]});}
            var Q42;
            Q42=makeQuery(id+"F1.opExtrude","CAP_EDGE",EDGE,{"disambiguationData":[OSD([sQuery(id+"F0.wireOp",EDGE,"E11")])],"isStart":true});
            var Q43;
            Q43=makeQuery(id+"F1.opExtrude","CAP_EDGE",EDGE,{"disambiguationData":[OSD([sQuery(id+"F0.wireOp",EDGE,"E11")])],"isStart":false});
            var Q44;
            {var subQ0=sQuery(id+"F0.wireOp",EDGE,"E11");var subQ1=sQuery(id+"F0.wireOp",EDGE,"E10");Q44=makeQuery(id+"F2.opFillet","BLEND_EDGE",EDGE,{"blendedFrom":[makeQuery(id+"F1.opExtrude","SWEPT_EDGE",EDGE,{"disambiguationData":[OSD([subQ1,subQ0])]}),makeQuery(id+"F1.opExtrude","CAP_FACE",FACE,{"disambiguationData":[OSD([sQuery(id+"F0.wireOp",EDGE,"E0"),sQuery(id+"F0.wireOp",EDGE,"E1"),sQuery(id+"F0.wireOp",EDGE,"E2"),sQuery(id+"F0.wireOp",EDGE,"E3"),sQuery(id+"F0.wireOp",EDGE,"E4"),sQuery(id+"F0.wireOp",EDGE,"E5"),sQuery(id+"F0.wireOp",EDGE,"E6"),sQuery(id+"F0.wireOp",EDGE,"E7"),sQuery(id+"F0.wireOp",EDGE,"E8"),sQuery(id+"F0.wireOp",EDGE,"E9"),subQ1,subQ0])],"isStart":false})],"blendedInto":[makeQuery(id+"F1.opExtrude","CAP_FACE",FACE,{"disambiguationData":[OSD([sQuery(id+"F0.wireOp",EDGE,"E0"),sQuery(id+"F0.wireOp",EDGE,"E1"),sQuery(id+"F0.wireOp",EDGE,"E2"),sQuery(id+"F0.wireOp",EDGE,"E3"),sQuery(id+"F0.wireOp",EDGE,"E4"),sQuery(id+"F0.wireOp",EDGE,"E5"),sQuery(id+"F0.wireOp",EDGE,"E6"),sQuery(id+"F0.wireOp",EDGE,"E7"),sQuery(id+"F0.wireOp",EDGE,"E8"),sQuery(id+"F0.wireOp",EDGE,"E9"),subQ1,subQ0])],"isStart":false})]});}
            var Q45;
            Q45=makeQuery(id+"F1.opExtrude","CAP_EDGE",EDGE,{"disambiguationData":[OSD([sQuery(id+"F0.wireOp",EDGE,"E10")])],"isStart":false});
            var Q46;
            {var subQ0=sQuery(id+"F0.wireOp",EDGE,"E10");var subQ1=sQuery(id+"F0.wireOp",EDGE,"E9");Q46=makeQuery(id+"F2.opFillet","BLEND_EDGE",EDGE,{"blendedFrom":[makeQuery(id+"F1.opExtrude","SWEPT_EDGE",EDGE,{"disambiguationData":[OSD([subQ1,subQ0])]}),makeQuery(id+"F1.opExtrude","CAP_FACE",FACE,{"disambiguationData":[OSD([sQuery(id+"F0.wireOp",EDGE,"E0"),sQuery(id+"F0.wireOp",EDGE,"E1"),sQuery(id+"F0.wireOp",EDGE,"E2"),sQuery(id+"F0.wireOp",EDGE,"E3"),sQuery(id+"F0.wireOp",EDGE,"E4"),sQuery(id+"F0.wireOp",EDGE,"E5"),sQuery(id+"F0.wireOp",EDGE,"E6"),sQuery(id+"F0.wireOp",EDGE,"E7"),sQuery(id+"F0.wireOp",EDGE,"E8"),subQ1,subQ0,sQuery(id+"F0.wireOp",EDGE,"E11")])],"isStart":false})],"blendedInto":[makeQuery(id+"F1.opExtrude","CAP_FACE",FACE,{"disambiguationData":[OSD([sQuery(id+"F0.wireOp",EDGE,"E0"),sQuery(id+"F0.wireOp",EDGE,"E1"),sQuery(id+"F0.wireOp",EDGE,"E2"),sQuery(id+"F0.wireOp",EDGE,"E3"),sQuery(id+"F0.wireOp",EDGE,"E4"),sQuery(id+"F0.wireOp",EDGE,"E5"),sQuery(id+"F0.wireOp",EDGE,"E6"),sQuery(id+"F0.wireOp",EDGE,"E7"),sQuery(id+"F0.wireOp",EDGE,"E8"),subQ1,subQ0,sQuery(id+"F0.wireOp",EDGE,"E11")])],"isStart":false})]});}
            var Q47;
            Q47=makeQuery(id+"F1.opExtrude","CAP_EDGE",EDGE,{"disambiguationData":[OSD([sQuery(id+"F0.wireOp",EDGE,"E9")])],"isStart":false});
            var Q48;
            Q48=makeQuery(id+"F3.opFillet","BLEND_EDGE",EDGE,{"blendedFrom":[makeQuery(id+"F1.opExtrude","CAP_EDGE",EDGE,{"disambiguationData":[OSD([sQuery(id+"F0.wireOp",EDGE,"E8")])],"isStart":false}),makeQuery(id+"F1.opExtrude","SWEPT_FACE",FACE,{"disambiguationData":[OSD([sQuery(id+"F0.wireOp",EDGE,"E9")])]})],"blendedInto":[makeQuery(id+"F1.opExtrude","SWEPT_FACE",FACE,{"disambiguationData":[OSD([sQuery(id+"F0.wireOp",EDGE,"E9")])]})]});
            var Q49;
            {var subQ0=sQuery(id+"F0.wireOp",EDGE,"E8");Q49=makeQuery(id+"F3.opFillet","BLEND_EDGE",EDGE,{"blendedFrom":[makeQuery(id+"F1.opExtrude","CAP_EDGE",EDGE,{"disambiguationData":[OSD([subQ0])],"isStart":false}),makeQuery(id+"F2.opFillet","BLEND_FACE",FACE,{"disambiguationData":[OSD([subQ0,sQuery(id+"F0.wireOp",EDGE,"E9")])]})],"blendedInto":[makeQuery(id+"F2.opFillet","BLEND_FACE",FACE,{"disambiguationData":[OSD([subQ0,sQuery(id+"F0.wireOp",EDGE,"E9")])]})]});}
            var Q50;
            Q50=makeQuery(id+"F3.opFillet","BLEND_EDGE",EDGE,{"blendedFrom":[makeQuery(id+"F1.opExtrude","CAP_EDGE",EDGE,{"disambiguationData":[OSD([sQuery(id+"F0.wireOp",EDGE,"E4")])],"isStart":true}),makeQuery(id+"F1.opExtrude","SWEPT_FACE",FACE,{"disambiguationData":[OSD([sQuery(id+"F0.wireOp",EDGE,"E11")])]})],"blendedInto":[makeQuery(id+"F1.opExtrude","SWEPT_FACE",FACE,{"disambiguationData":[OSD([sQuery(id+"F0.wireOp",EDGE,"E11")])]})]});
            var Q51;
            {var subQ0=sQuery(id+"F0.wireOp",EDGE,"E4");Q51=makeQuery(id+"F3.opFillet","BLEND_EDGE",EDGE,{"blendedFrom":[makeQuery(id+"F1.opExtrude","CAP_EDGE",EDGE,{"disambiguationData":[OSD([subQ0])],"isStart":true}),makeQuery(id+"F2.opFillet","BLEND_FACE",FACE,{"disambiguationData":[OSD([subQ0,sQuery(id+"F0.wireOp",EDGE,"E11")])]})],"blendedInto":[makeQuery(id+"F2.opFillet","BLEND_FACE",FACE,{"disambiguationData":[OSD([subQ0,sQuery(id+"F0.wireOp",EDGE,"E11")])]})]});}
            var Q52;
            Q52=makeQuery(id+"F3.opFillet","BLEND_EDGE",EDGE,{"blendedFrom":[makeQuery(id+"F1.opExtrude","CAP_EDGE",EDGE,{"disambiguationData":[OSD([sQuery(id+"F0.wireOp",EDGE,"E4")])],"isStart":false}),makeQuery(id+"F1.opExtrude","SWEPT_FACE",FACE,{"disambiguationData":[OSD([sQuery(id+"F0.wireOp",EDGE,"E11")])]})],"blendedInto":[makeQuery(id+"F1.opExtrude","SWEPT_FACE",FACE,{"disambiguationData":[OSD([sQuery(id+"F0.wireOp",EDGE,"E11")])]})]});
            var Q53;
            {var subQ0=sQuery(id+"F0.wireOp",EDGE,"E4");Q53=makeQuery(id+"F3.opFillet","BLEND_EDGE",EDGE,{"blendedFrom":[makeQuery(id+"F1.opExtrude","CAP_EDGE",EDGE,{"disambiguationData":[OSD([subQ0])],"isStart":false}),makeQuery(id+"F2.opFillet","BLEND_FACE",FACE,{"disambiguationData":[OSD([subQ0,sQuery(id+"F0.wireOp",EDGE,"E11")])]})],"blendedInto":[makeQuery(id+"F2.opFillet","BLEND_FACE",FACE,{"disambiguationData":[OSD([subQ0,sQuery(id+"F0.wireOp",EDGE,"E11")])]})]});}
            fillet(context, id + "F4", {"entities" : qUnion([Q0, Q1, Q2, Q3, Q4, Q5, Q6, Q7, Q8, Q9, Q10, Q11, Q12, Q13, Q14, Q15, Q16, Q17, Q18, Q19, Q20, Q21, Q22, Q23, Q24, Q25, Q26, Q27, Q28, Q29, Q30, Q31, Q32, Q33, Q34, Q35, Q36, Q37, Q38, Q39, Q40, Q41, Q42, Q43, Q44, Q45, Q46, Q47, Q48, Q49, Q50, Q51, Q52, Q53]), "radius" : 0.5 * mm, "allowEdgeOverflow" : false});
        }
        {
            var Q0;
            Q0=makeQuery(id+"F1.opExtrude","SWEPT_FACE",FACE,{"disambiguationData":[OSD([sQuery(id+"F0.wireOp",EDGE,"E7")])]});
            var sketch = newSketch(context, id + "F5", { "sketchPlane" : qUnion([Q0])});
            skPoint(sketch, "E12.endSnap0", {"position": v(1, 2) * mm});
            skCircle(sketch, "E13", {"center": v(1.95, 2) * mm, "radius": 0.45 * mm});
            skSolve(sketch);
        }
        {
            var Q0;
            Q0=makeQuery(id+"F1.opExtrude","SWEPT_FACE",FACE,{"disambiguationData":[OSD([sQuery(id+"F0.wireOp",EDGE,"E5")])]});
            var sketch = newSketch(context, id + "F6", { "sketchPlane" : qUnion([Q0])});
            skCircle(sketch, "E14", {"center": v(12.05, 2) * mm, "radius": 0.45 * mm});
            skSolve(sketch);
        }
        {
            var Q0;
            Q0=makeQuery(id+"F6.imprint","IMPRINT",FACE,{"disambiguationData":[TD([[makeQuery(id+"F6.imprint","IMPRINT",EDGE,{"derivedFrom":sQuery(id+"F6.wireOp",EDGE,"E14")}),1.0]])]});
            extrude(context, id + "F7", {"entities" : qUnion([Q0]), "operationType" : NewBodyOperationType.ADD, "depth" : 5 * mm, "offsetDistance" : 25 * mm, "hasSecondDirection" : true, "secondDirectionOppositeDirection" : true, "secondDirectionDepth" : 28 * mm});
        }
        {
            var Q0;
            Q0=makeQuery(id+"F5.imprint","IMPRINT",FACE,{"disambiguationData":[TD([[makeQuery(id+"F5.imprint","IMPRINT",EDGE,{"derivedFrom":sQuery(id+"F5.wireOp",EDGE,"E13")}),1.0]])]});
            extrude(context, id + "F8", {"entities" : qUnion([Q0]), "operationType" : NewBodyOperationType.ADD, "depth" : 9.6 * mm, "offsetDistance" : 25 * mm, "hasSecondDirection" : true, "secondDirectionOppositeDirection" : true, "secondDirectionDepth" : 23.4 * mm});
        }
    });
